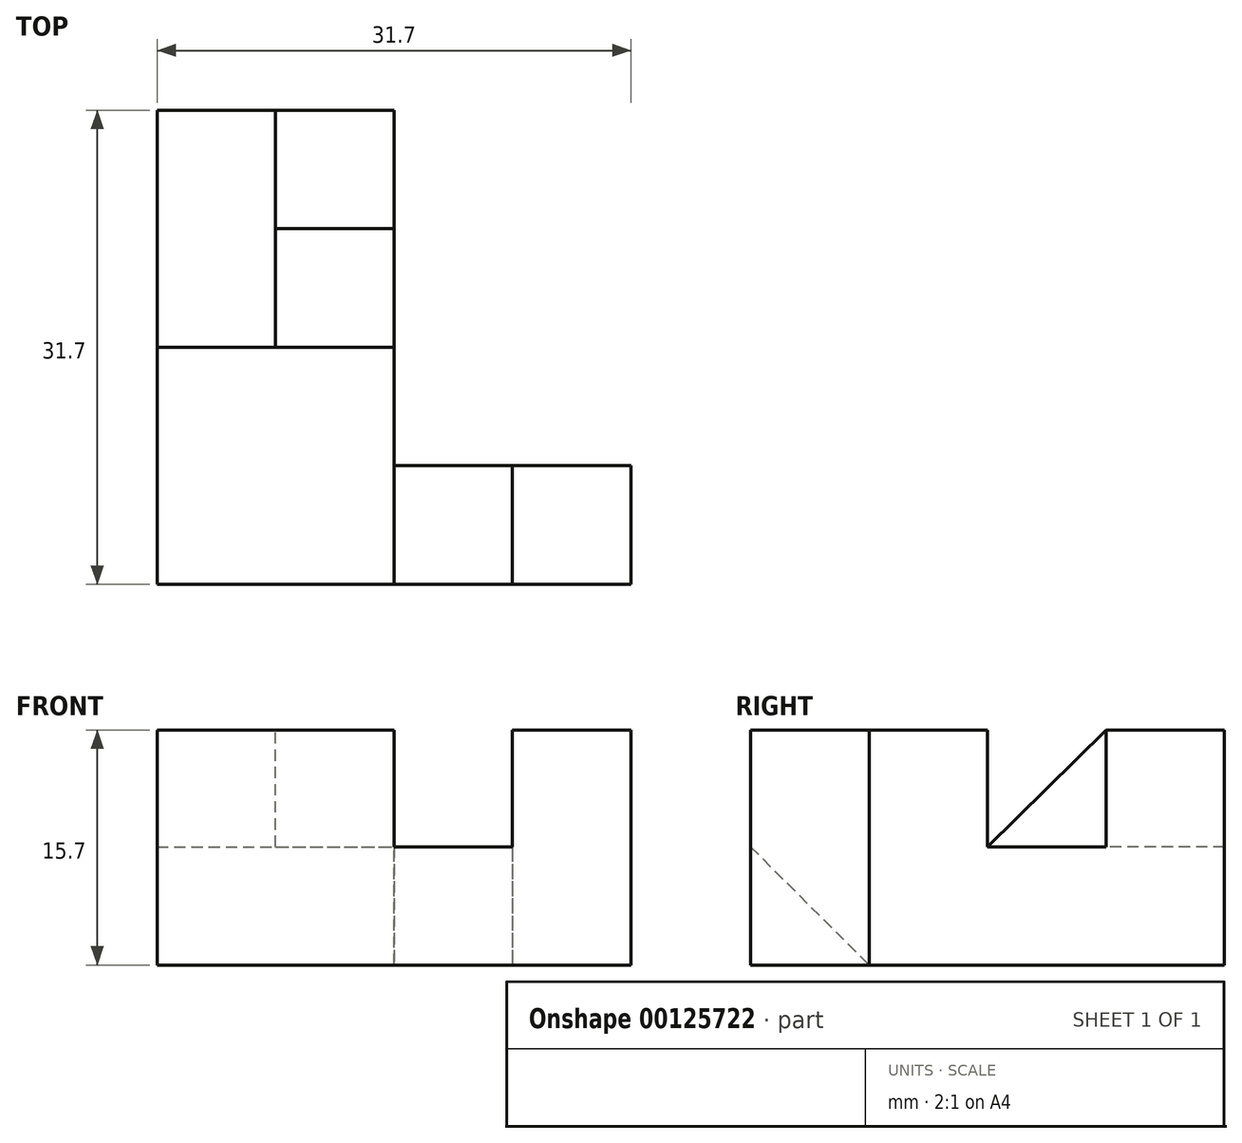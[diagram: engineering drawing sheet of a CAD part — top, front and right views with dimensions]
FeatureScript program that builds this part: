
annotation { "Feature Type Name" : "Feature", "Feature Type Description" : "" }
export const myFeature = defineFeature(function(context is Context, id is Id, definition is map)
    precondition{}
    {
        {
            var Q0;
            Q0=qCreatedBy(makeId("Top.planeOp"),FACE);
            var sketch = newSketch(context, id + "F0", { "sketchPlane" : qUnion([Q0])});
            skLineSegment(sketch, "E0", {"start": v(0, 0) * mm, "end": v(0, -31.7) * mm});
            skLineSegment(sketch, "E1", {"start": v(0, 0) * mm, "end": v(31.7, 0) * mm});
            skLineSegment(sketch, "E2", {"start": v(31.7, 0) * mm, "end": v(31.7, -31.7) * mm});
            skLineSegment(sketch, "E3", {"start": v(0, -31.7) * mm, "end": v(31.7, -31.7) * mm});
            skSolve(sketch);
        }
        {
            var Q0;
            Q0=qSketchRegion(id+"F0",true);
            extrude(context, id + "F1", {"entities" : qUnion([Q0]), "depth" : 7.9 * mm});
        }
        {
            var Q0;
            Q0=makeQuery(id+"F1.opExtrude","CAP_FACE",FACE,{"disambiguationData":[OSD([sQuery(id+"F0.wireOp",EDGE,"E0"),sQuery(id+"F0.wireOp",EDGE,"E1"),sQuery(id+"F0.wireOp",EDGE,"E2"),sQuery(id+"F0.wireOp",EDGE,"E3")])],"isStart":false});
            var sketch = newSketch(context, id + "F2", { "sketchPlane" : qUnion([Q0])});
            skLineSegment(sketch, "E4", {"start": v(15.85, -15.85) * mm, "end": v(15.85, -31.7) * mm});
            skLineSegment(sketch, "E5", {"start": v(0, -15.85) * mm, "end": v(15.85, -15.85) * mm});
            skSolve(sketch);
        }
        {
            var Q0;
            Q0=qSketchRegion(id+"F2",true);
            var Q1;
            {var subQ0=sQuery(id+"F2.wireOp",EDGE,"E4");Q1=makeQuery(id+"F2.imprint","IMPRINT",FACE,{"disambiguationData":[TD([[makeQuery(id+"F2.imprint","IMPRINT",EDGE,{"derivedFrom":subQ0}),-1.0]])]});}
            extrude(context, id + "F3", {"entities" : qUnion([Q0, Q1]), "operationType" : NewBodyOperationType.ADD, "depth" : 7.8 * mm});
        }
        {
            var Q0;
            Q0=makeQuery(id+"F1.opExtrude","CAP_FACE",FACE,{"disambiguationData":[OSD([sQuery(id+"F0.wireOp",EDGE,"E0"),sQuery(id+"F0.wireOp",EDGE,"E1"),sQuery(id+"F0.wireOp",EDGE,"E2"),sQuery(id+"F0.wireOp",EDGE,"E3")])],"isStart":false});
            var sketch = newSketch(context, id + "F4", { "sketchPlane" : qUnion([Q0])});
            skLineSegment(sketch, "E6", {"start": v(0, -15.85) * mm, "end": v(0, 0) * mm});
            skLineSegment(sketch, "E7", {"start": v(0, 0) * mm, "end": v(15.85, 0) * mm});
            skLineSegment(sketch, "E8", {"start": v(15.85, 0) * mm, "end": v(15.85, -15.85) * mm});
            skLineSegment(sketch, "E9", {"start": v(15.85, -23.77) * mm, "end": v(31.7, -23.77) * mm});
            skLineSegment(sketch, "E10", {"start": v(31.7, -23.77) * mm, "end": v(31.7, -31.7) * mm});
            skLineSegment(sketch, "E11", {"start": v(31.7, -31.7) * mm, "end": v(15.85, -31.7) * mm});
            skLineSegment(sketch, "E12", {"start": v(15.85, -31.7) * mm, "end": v(15.85, -23.77) * mm});
            skSolve(sketch);
        }
        {
            var Q0;
            {var subQ4=sQuery(id+"F4.wireOp",EDGE,"E8");Q0=makeQuery(id+"F4.imprint","IMPRINT",FACE,{"disambiguationData":[TD([[makeQuery(id+"F4.imprint","IMPRINT",EDGE,{"derivedFrom":subQ4}),1.0]])]});}
            extrude(context, id + "F5", {"entities" : qUnion([Q0]), "operationType" : NewBodyOperationType.REMOVE, "oppositeDirection" : true, "depth" : 25 * mm});
        }
        {
            var Q0;
            {var subQ1=sQuery(id+"F0.wireOp",EDGE,"E3");var subQ2=sQuery(id+"F0.wireOp",EDGE,"E2");Q0=makeQuery(id+"F5.boolean.opBoolean","SPLIT",FACE,{"disambiguationData":[TD([makeQuery(id+"F1.opExtrude","SWEPT_FACE",FACE,{"disambiguationData":[OSD([subQ2])]})])],"derivedFrom":makeQuery(id+"F1.opExtrude","CAP_FACE",FACE,{"disambiguationData":[OSD([sQuery(id+"F0.wireOp",EDGE,"E0"),sQuery(id+"F0.wireOp",EDGE,"E1"),subQ2,subQ1])],"isStart":false})});}
            var sketch = newSketch(context, id + "F6", { "sketchPlane" : qUnion([Q0])});
            skLineSegment(sketch, "E13", {"start": v(23.77, -23.77) * mm, "end": v(23.77, -31.7) * mm});
            skLineSegment(sketch, "E14", {"start": v(23.77, -31.7) * mm, "end": v(31.7, -31.7) * mm});
            skLineSegment(sketch, "E15", {"start": v(31.7, -31.7) * mm, "end": v(31.7, -23.77) * mm});
            skLineSegment(sketch, "E16", {"start": v(31.7, -23.77) * mm, "end": v(23.77, -23.77) * mm});
            skSolve(sketch);
        }
        {
            var Q0;
            Q0=makeQuery(id+"F6.imprint","IMPRINT",FACE,{"disambiguationData":[TD([[makeQuery(id+"F6.imprint","IMPRINT",EDGE,{"derivedFrom":sQuery(id+"F6.wireOp",EDGE,"E13")}),1.0]])]});
            extrude(context, id + "F7", {"entities" : qUnion([Q0]), "operationType" : NewBodyOperationType.ADD, "depth" : 7.8 * mm});
        }
        {
            var Q0;
            {var subQ0=sQuery(id+"F0.wireOp",EDGE,"E1");var subQ2=sQuery(id+"F0.wireOp",EDGE,"E0");Q0=makeQuery(id+"F5.boolean.opBoolean","SPLIT",FACE,{"disambiguationData":[TD([makeQuery(id+"F1.opExtrude","SWEPT_FACE",FACE,{"disambiguationData":[OSD([subQ2])]})])],"derivedFrom":makeQuery(id+"F1.opExtrude","CAP_FACE",FACE,{"disambiguationData":[OSD([subQ2,subQ0,sQuery(id+"F0.wireOp",EDGE,"E2"),sQuery(id+"F0.wireOp",EDGE,"E3")])],"isStart":false})});}
            var sketch = newSketch(context, id + "F8", { "sketchPlane" : qUnion([Q0])});
            skLineSegment(sketch, "E17", {"start": v(7.92, 0) * mm, "end": v(7.92, -7.92) * mm});
            skPoint(sketch, "E17.endSnap0", {"position": v(15.85, -7.92) * mm});
            skLineSegment(sketch, "E18", {"start": v(7.92, -7.92) * mm, "end": v(15.85, -7.92) * mm});
            skLineSegment(sketch, "E19", {"start": v(15.85, 0) * mm, "end": v(7.92, 0) * mm});
            skSolve(sketch);
        }
        {
            var Q0;
            Q0=makeQuery(id+"F8.imprint","IMPRINT",FACE,{"disambiguationData":[TD([[makeQuery(id+"F8.imprint","IMPRINT",EDGE,{"derivedFrom":sQuery(id+"F8.wireOp",EDGE,"E17")}),1.0]])]});
            extrude(context, id + "F9", {"entities" : qUnion([Q0]), "operationType" : NewBodyOperationType.ADD, "depth" : 7.8 * mm});
        }
        {
            var Q0;
            {var subQ0=sQuery(id+"F4.wireOp",EDGE,"E8");var subQ1=sQuery(id+"F2.wireOp",EDGE,"E4");Q0=makeQuery(id+"F9.boolean.opBoolean","MERGE",FACE,{"derivedFrom":[makeQuery(id+"F5.boolean.opBoolean","MERGE",FACE,{"derivedFrom":[makeQuery(id+"F3.opExtrude","SWEPT_FACE",FACE,{"disambiguationData":[OSD([subQ1])]}),makeQuery(id+"F5.opExtrude","SWEPT_FACE",FACE,{"disambiguationData":[OSD([subQ1,subQ0])]})]}),makeQuery(id+"F9.opExtrude","SWEPT_FACE",FACE,{"disambiguationData":[OSD([subQ1,subQ0])]})]});}
            var sketch = newSketch(context, id + "F10", { "sketchPlane" : qUnion([Q0])});
            skLineSegment(sketch, "E20", {"start": v(-7.92, 15.7) * mm, "end": v(-15.85, 7.9) * mm});
            skSolve(sketch);
        }
        {
            var Q0;
            Q0=qSketchRegion(id+"F10",true);
            var Q1;
            Q1=makeQuery(id+"F10.imprint","IMPRINT",FACE,{"disambiguationData":[TD([[makeQuery(id+"F10.imprint","IMPRINT",EDGE,{"derivedFrom":sQuery(id+"F10.wireOp",EDGE,"E20")}),1.0]])]});
            var Q2;
            Q2=makeQuery(id+"F9.opExtrude","SWEPT_FACE",FACE,{"disambiguationData":[OSD([sQuery(id+"F8.wireOp",EDGE,"E17")])]});
            extrude(context, id + "F11", {"entities" : qUnion([Q0, Q1]), "endBound" : BoundingType.UP_TO_SURFACE, "oppositeDirection" : true, "endBoundEntityFace" : qUnion([Q2]), "depth" : 25 * mm});
        }
        {
            var Q0;
            {var subQ0=sQuery(id+"F4.wireOp",EDGE,"E8");var subQ1=sQuery(id+"F2.wireOp",EDGE,"E4");Q0=makeQuery(id+"F9.boolean.opBoolean","MERGE",FACE,{"derivedFrom":[makeQuery(id+"F5.boolean.opBoolean","MERGE",FACE,{"derivedFrom":[makeQuery(id+"F3.opExtrude","SWEPT_FACE",FACE,{"disambiguationData":[OSD([subQ1])]}),makeQuery(id+"F5.opExtrude","SWEPT_FACE",FACE,{"disambiguationData":[OSD([subQ1,subQ0])]})]}),makeQuery(id+"F9.opExtrude","SWEPT_FACE",FACE,{"disambiguationData":[OSD([subQ1,subQ0])]})]});}
            var sketch = newSketch(context, id + "F12", { "sketchPlane" : qUnion([Q0])});
            skLineSegment(sketch, "E21", {"start": v(-31.7, 7.9) * mm, "end": v(-23.77, 0) * mm});
            skLineSegment(sketch, "E22", {"start": v(-23.77, 0) * mm, "end": v(-23.77, 7.9) * mm});
            skLineSegment(sketch, "E23", {"start": v(-23.77, 7.9) * mm, "end": v(-31.7, 7.9) * mm});
            skSolve(sketch);
        }
        {
            var Q0;
            Q0=qSketchRegion(id+"F12",true);
            var Q1;
            Q1=makeQuery(id+"F7.opExtrude","SWEPT_FACE",FACE,{"disambiguationData":[OSD([sQuery(id+"F6.wireOp",EDGE,"E13")])]});
            extrude(context, id + "F13", {"entities" : qUnion([Q0]), "operationType" : NewBodyOperationType.REMOVE, "endBound" : BoundingType.UP_TO_SURFACE, "endBoundEntityFace" : qUnion([Q1]), "depth" : 25 * mm});
        }
    });
